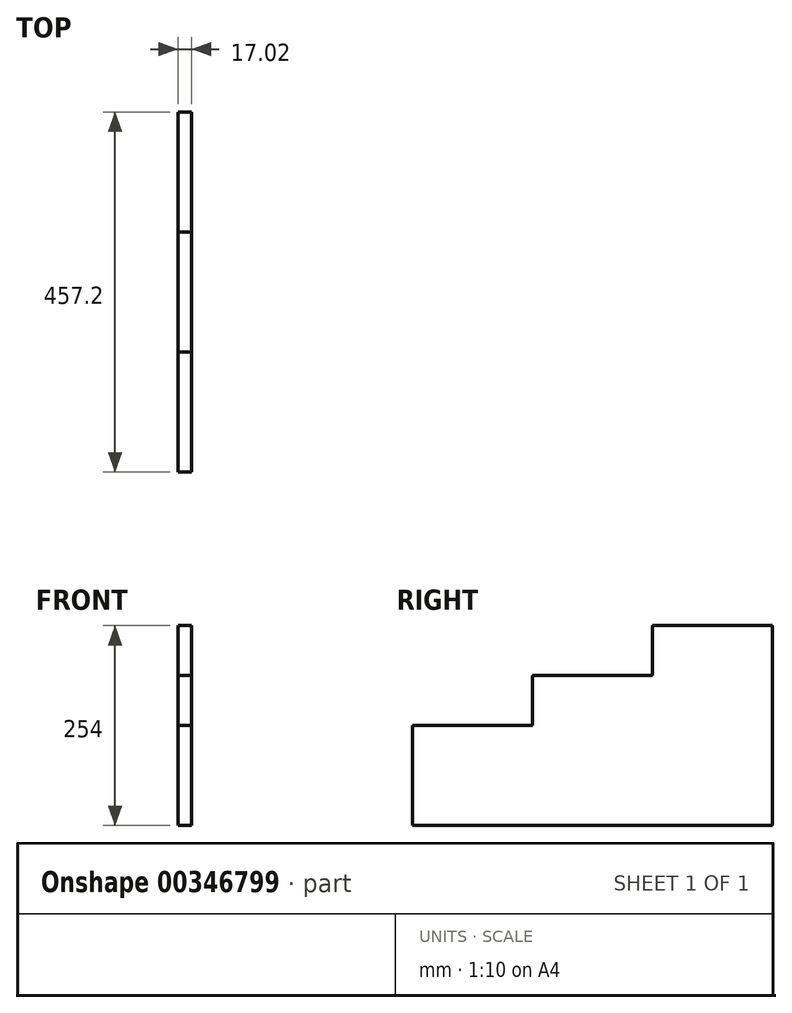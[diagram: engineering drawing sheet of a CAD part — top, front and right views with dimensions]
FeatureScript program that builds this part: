
annotation { "Feature Type Name" : "Feature", "Feature Type Description" : "" }
export const myFeature = defineFeature(function(context is Context, id is Id, definition is map)
    precondition{}
    {
        {
            var Q0;
            Q0=qCreatedBy(makeId("Right.planeOp"),FACE);
            var sketch = newSketch(context, id + "F0", { "sketchPlane" : qUnion([Q0])});
            skLineSegment(sketch, "E0.bottom", {"start": v(457.2, 254) * mm, "end": v(304.8, 254) * mm});
            skLineSegment(sketch, "E0.top", {"start": v(457.2, 0) * mm, "end": v(0, 0) * mm});
            skLineSegment(sketch, "E0.left", {"start": v(457.2, 254) * mm, "end": v(457.2, 0) * mm});
            skLineSegment(sketch, "E0.right", {"start": v(0, 127) * mm, "end": v(0, 0) * mm});
            skLineSegment(sketch, "E1", {"start": v(304.8, 254) * mm, "end": v(304.8, 190.5) * mm});
            skLineSegment(sketch, "E2", {"start": v(304.8, 190.5) * mm, "end": v(152.4, 190.5) * mm});
            skLineSegment(sketch, "E3", {"start": v(152.4, 190.5) * mm, "end": v(152.4, 127) * mm});
            skLineSegment(sketch, "E4", {"start": v(152.4, 127) * mm, "end": v(0, 127) * mm});
            skSolve(sketch);
        }
        {
            var Q0;
            Q0=makeQuery(id+"F0.imprint","IMPRINT",FACE,{"disambiguationData":[TD([[makeQuery(id+"F0.imprint","IMPRINT",EDGE,{"derivedFrom":sQuery(id+"F0.wireOp",EDGE,"E0.bottom")}),1.0]])]});
            extrude(context, id + "F1", {"entities" : qUnion([Q0]), "depth" : 17.02 * mm});
        }
    });
